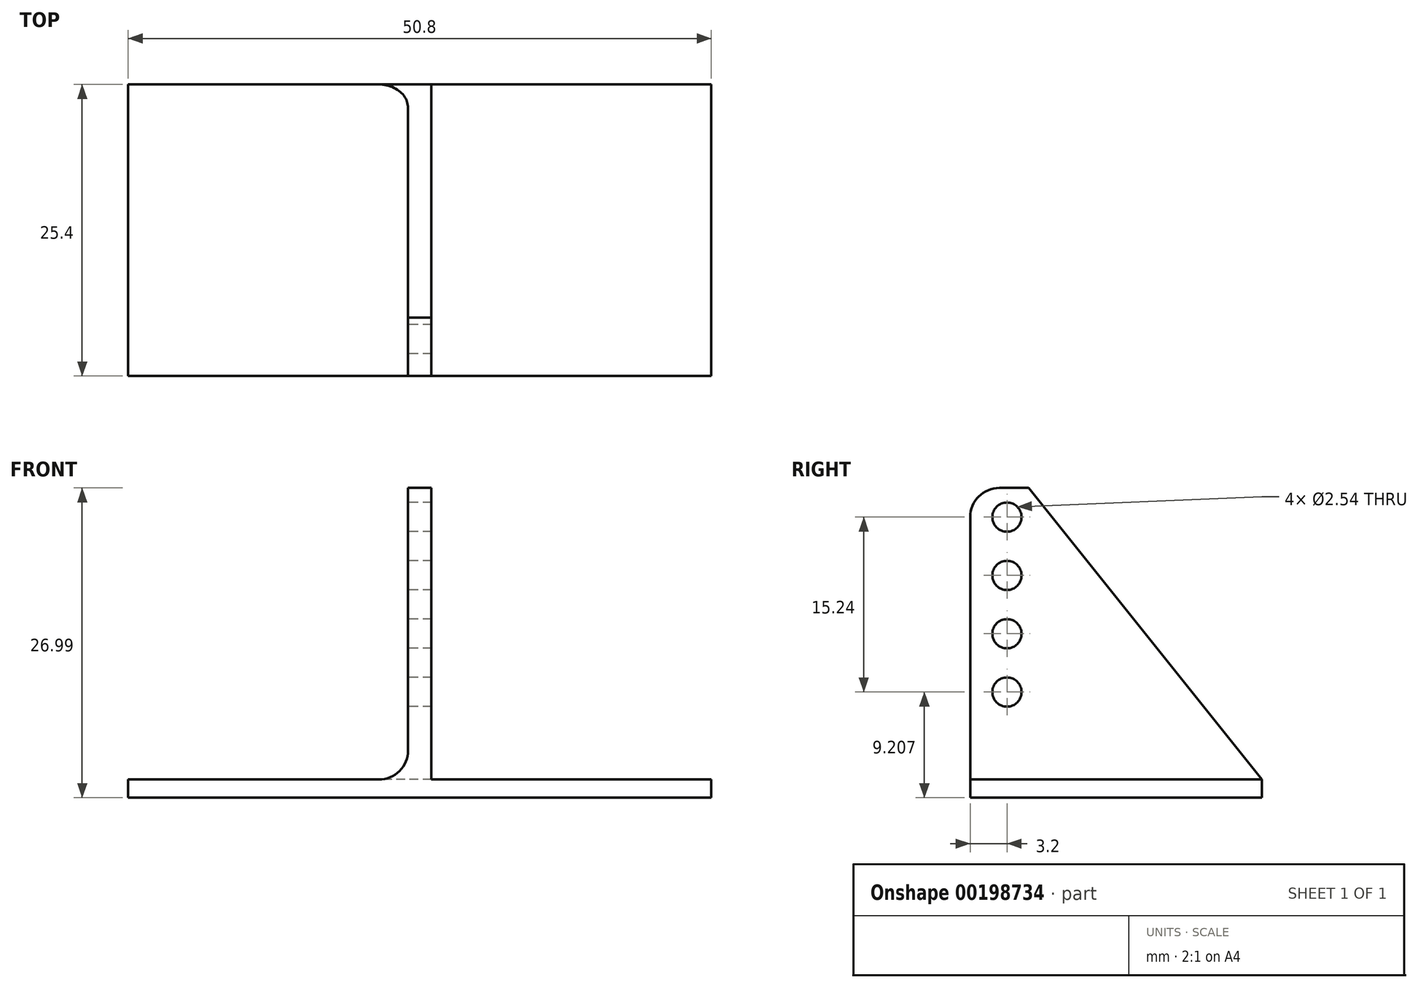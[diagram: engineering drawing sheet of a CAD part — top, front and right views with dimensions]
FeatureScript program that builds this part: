
annotation { "Feature Type Name" : "Feature", "Feature Type Description" : "" }
export const myFeature = defineFeature(function(context is Context, id is Id, definition is map)
    precondition{}
    {
        {
            var Q0;
            Q0=qCreatedBy(makeId("Top.planeOp"),FACE);
            var sketch = newSketch(context, id + "F0", { "sketchPlane" : qUnion([Q0])});
            skLineSegment(sketch, "E0.bottom", {"start": v(25.4, -12.7) * mm, "end": v(-25.4, -12.7) * mm});
            skLineSegment(sketch, "E0.top", {"start": v(25.4, 12.7) * mm, "end": v(-25.4, 12.7) * mm});
            skLineSegment(sketch, "E0.left", {"start": v(25.4, -12.7) * mm, "end": v(25.4, 12.7) * mm});
            skLineSegment(sketch, "E0.right", {"start": v(-25.4, -12.7) * mm, "end": v(-25.4, 12.7) * mm});
            skPoint(sketch, "E0.middle", {"position": v(0, 0) * mm});
            skSolve(sketch);
        }
        {
            var Q0;
            Q0 = qSketchRegion(id + "F0", true);
            extrude(context, id + "F1", {"entities" : qUnion([Q0]), "depth" : 1.59 * mm});
        }
        {
            var Q0;
            Q0=makeQuery(id+"F1.opExtrude","CAP_FACE",FACE,{"disambiguationData":[OSD([sQuery(id+"F0.wireOp",EDGE,"E0.bottom"),sQuery(id+"F0.wireOp",EDGE,"E0.top"),sQuery(id+"F0.wireOp",EDGE,"E0.left"),sQuery(id+"F0.wireOp",EDGE,"E0.right")])],"isStart":false});
            var sketch = newSketch(context, id + "F2", { "sketchPlane" : qUnion([Q0])});
            skLineSegment(sketch, "E1.bottom", {"start": v(1.02, -12.7) * mm, "end": v(-1.02, -12.7) * mm});
            skLineSegment(sketch, "E1.top", {"start": v(1.02, 12.7) * mm, "end": v(-1.02, 12.7) * mm});
            skLineSegment(sketch, "E1.left", {"start": v(1.02, -12.7) * mm, "end": v(1.02, 12.7) * mm});
            skLineSegment(sketch, "E1.right", {"start": v(-1.02, -12.7) * mm, "end": v(-1.02, 12.7) * mm});
            skPoint(sketch, "E1.middle", {"position": v(0, 0) * mm});
            skSolve(sketch);
        }
        {
            var Q0;
            Q0 = qSketchRegion(id + "F2", true);
            extrude(context, id + "F3", {"entities" : qUnion([Q0]), "operationType" : NewBodyOperationType.ADD, "depth" : 25.4 * mm});
        }
        {
            var Q0;
            Q0=makeQuery(id+"F3.opExtrude","SWEPT_FACE",FACE,{"disambiguationData":[OSD([sQuery(id+"F2.wireOp",EDGE,"E1.right")])]});
            var sketch = newSketch(context, id + "F4", { "sketchPlane" : qUnion([Q0])});
            skLineSegment(sketch, "E2", {"start": v(-12.7, 1.59) * mm, "end": v(7.62, 26.99) * mm});
            skLineSegment(sketch, "E3", {"start": v(7.62, 26.99) * mm, "end": v(-12.7, 26.99) * mm});
            skLineSegment(sketch, "E4", {"start": v(-12.7, 26.99) * mm, "end": v(-12.7, 1.59) * mm});
            skSolve(sketch);
        }
        {
            var Q0;
            Q0 = qSketchRegion(id + "F4", true);
            extrude(context, id + "F5", {"entities" : qUnion([Q0]), "operationType" : NewBodyOperationType.REMOVE, "oppositeDirection" : true, "depth" : 25.4 * mm});
        }
        {
            var Q0;
            Q0=makeQuery(id+"F3.opExtrude","CAP_EDGE",EDGE,{"disambiguationData":[OSD([sQuery(id+"F2.wireOp",EDGE,"E1.right")])],"isStart":true});
            var Q1;
            Q1=makeQuery(id+"F3.opExtrude","CAP_EDGE",EDGE,{"disambiguationData":[OSD([sQuery(id+"F2.wireOp",EDGE,"E1.left")])],"isStart":true});
            fillet(context, id + "F6", {"entities" : qUnion([Q0, Q1]), "radius" : 2.54 * mm, "tangentPropagation" : true, "allowEdgeOverflow" : false});
        }
        {
            var Q0;
            Q0=makeQuery(id+"F5.boolean.opBoolean","COPY",EDGE,{"derivedFrom":makeQuery(id+"F5.opExtrude","SWEPT_EDGE",EDGE,{"disambiguationData":[OSD([sQuery(id+"F2.wireOp",EDGE,"E1.right"),sQuery(id+"F4.wireOp",EDGE,"E2"),sQuery(id+"F4.wireOp",EDGE,"E3")])]})});
            var Q1;
            Q1=makeQuery(id+"F3.opExtrude","CAP_EDGE",EDGE,{"disambiguationData":[OSD([sQuery(id+"F2.wireOp",EDGE,"E1.bottom")])],"isStart":false});
            fillet(context, id + "F7", {"entities" : qUnion([Q0, Q1]), "radius" : 2.54 * mm, "tangentPropagation" : true, "allowEdgeOverflow" : false});
        }
        {
            var Q0;
            Q0=makeQuery(id+"F3.opExtrude","SWEPT_FACE",FACE,{"disambiguationData":[OSD([sQuery(id+"F2.wireOp",EDGE,"E1.right")])]});
            var sketch = newSketch(context, id + "F8", { "sketchPlane" : qUnion([Q0])});
            skCircle(sketch, "E5", {"center": v(9.5, 24.45) * mm, "radius": 1.27 * mm});
            skLineSegment(sketch, "E6", {"start": v(9.5, 26.99) * mm, "end": v(9.5, 1.43) * mm, "construction": true});
            skCircle(sketch, "E7.0.1.0", {"center": v(9.5, 19.37) * mm, "radius": 1.27 * mm});
            skCircle(sketch, "E7.0.2.0", {"center": v(9.5, 14.29) * mm, "radius": 1.27 * mm});
            skCircle(sketch, "E7.0.3.0", {"center": v(9.5, 9.2) * mm, "radius": 1.27 * mm});
            skLineSegment(sketch, "E7.direction1", {"start": v(9.5, 24.45) * mm, "end": v(34.9, 24.45) * mm, "construction": true});
            skLineSegment(sketch, "E7.direction2", {"start": v(9.5, 24.45) * mm, "end": v(9.5, 19.37) * mm, "construction": true});
            skSolve(sketch);
        }
        {
            var Q0;
            Q0 = qSketchRegion(id + "F8", true);
            extrude(context, id + "F9", {"entities" : qUnion([Q0]), "operationType" : NewBodyOperationType.REMOVE, "oppositeDirection" : true, "depth" : 25.4 * mm});
        }
    });
